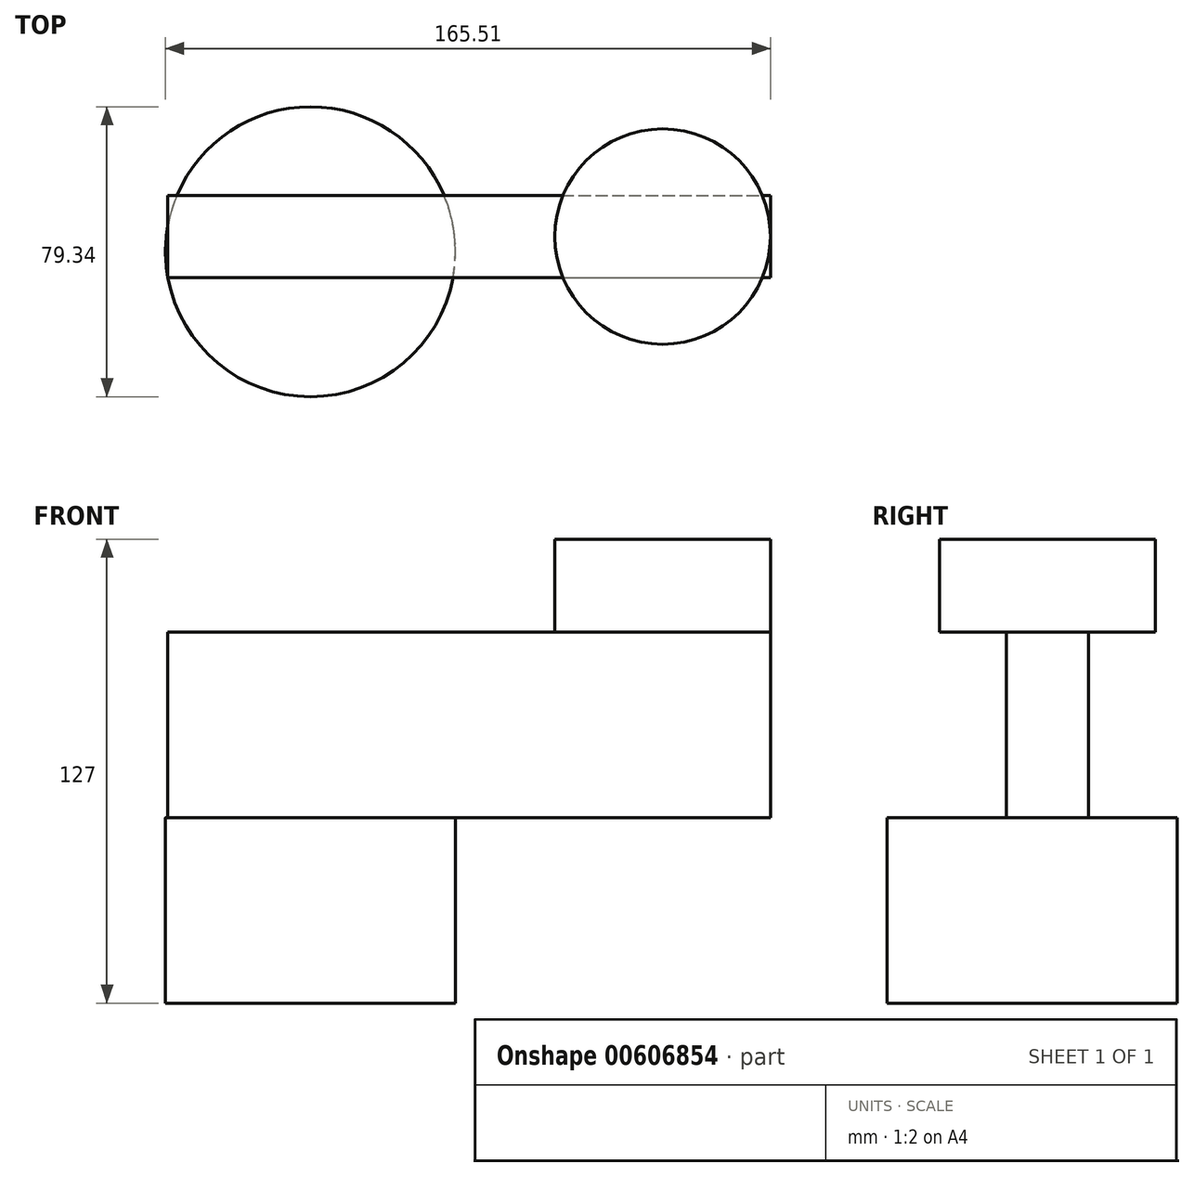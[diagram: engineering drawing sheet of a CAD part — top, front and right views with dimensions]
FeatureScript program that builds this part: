
annotation { "Feature Type Name" : "Feature", "Feature Type Description" : "" }
export const myFeature = defineFeature(function(context is Context, id is Id, definition is map)
    precondition{}
    {
        {
            var Q0;
            Q0=qCreatedBy(makeId("Top.planeOp"),FACE);
            var sketch = newSketch(context, id + "F0", { "sketchPlane" : qUnion([Q0])});
            skCircle(sketch, "E0", {"center": v(0, 0) * mm, "radius": 39.67 * mm});
            skSolve(sketch);
        }
        {
            var Q0;
            Q0=makeQuery(id+"F0.imprint","IMPRINT",FACE,{"disambiguationData":[TD([[makeQuery(id+"F0.imprint","IMPRINT",EDGE,{"derivedFrom":sQuery(id+"F0.wireOp",EDGE,"E0")}),1.0]])]});
            var Q1;
            Q1=sQuery(id+"F0.wireOp",EDGE,"E0");
            extrude(context, id + "F1", {"entities" : qUnion([Q0]), "surfaceEntities" : qUnion([Q1]), "depth" : 50.8 * mm, "offsetDistance" : 25.4 * mm});
        }
        {
            var Q0;
            Q0=makeQuery(id+"F1.opExtrude","CAP_FACE",FACE,{"disambiguationData":[OSD([sQuery(id+"F0.wireOp",EDGE,"E0")])],"isStart":false});
            var sketch = newSketch(context, id + "F2", { "sketchPlane" : qUnion([Q0])});
            skLineSegment(sketch, "E1.bottom", {"start": v(-39.03, -7.1) * mm, "end": v(125.84, -7.1) * mm});
            skLineSegment(sketch, "E1.top", {"start": v(-39.03, 15.4) * mm, "end": v(125.84, 15.4) * mm});
            skLineSegment(sketch, "E1.left", {"start": v(-39.03, -7.1) * mm, "end": v(-39.03, 15.4) * mm});
            skLineSegment(sketch, "E1.right", {"start": v(125.84, -7.1) * mm, "end": v(125.84, 15.4) * mm});
            skSolve(sketch);
        }
        {
            var Q0;
            Q0 = qSketchRegion(id + "F2", true);
            extrude(context, id + "F3", {"entities" : qUnion([Q0]), "operationType" : NewBodyOperationType.ADD, "depth" : 50.8 * mm, "offsetDistance" : 25.4 * mm});
        }
        {
            var Q0;
            Q0=makeQuery(id+"F3.opExtrude","CAP_FACE",FACE,{"disambiguationData":[OSD([sQuery(id+"F2.wireOp",EDGE,"E1.bottom"),sQuery(id+"F2.wireOp",EDGE,"E1.top"),sQuery(id+"F2.wireOp",EDGE,"E1.left"),sQuery(id+"F2.wireOp",EDGE,"E1.right")])],"isStart":false});
            var sketch = newSketch(context, id + "F4", { "sketchPlane" : qUnion([Q0])});
            skCircle(sketch, "E2", {"center": v(96.36, 4.14) * mm, "radius": 29.48 * mm});
            skPoint(sketch, "E2.centerSnap0", {"position": v(125.84, 4.14) * mm});
            skSolve(sketch);
        }
        {
            var Q0;
            Q0 = qSketchRegion(id + "F4", true);
            extrude(context, id + "F5", {"entities" : qUnion([Q0]), "operationType" : NewBodyOperationType.ADD, "depth" : 25.4 * mm, "offsetDistance" : 25.4 * mm});
        }
    });
